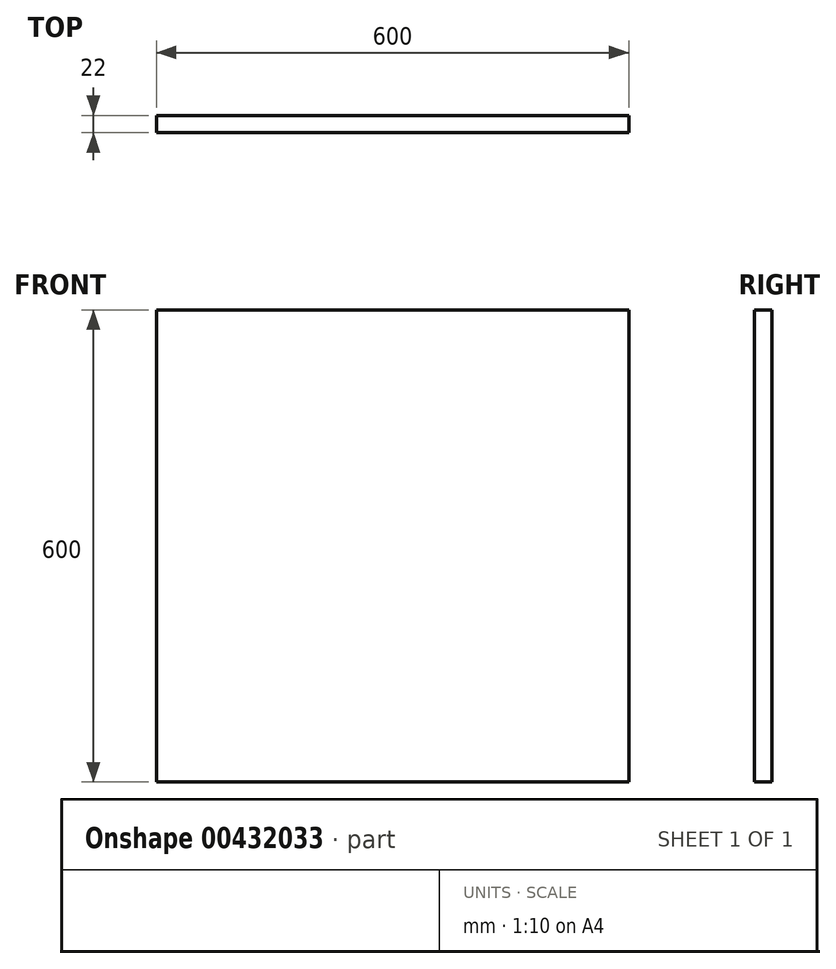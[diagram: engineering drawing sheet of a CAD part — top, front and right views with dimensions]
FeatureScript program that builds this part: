
annotation { "Feature Type Name" : "Feature", "Feature Type Description" : "" }
export const myFeature = defineFeature(function(context is Context, id is Id, definition is map)
    precondition{}
    {
        {
            var Q0;
            Q0=qCreatedBy(makeId("Front.planeOp"),FACE);
            var sketch = newSketch(context, id + "F0", { "sketchPlane" : qUnion([Q0])});
            skLineSegment(sketch, "E0.bottom", {"start": v(0, 0) * mm, "end": v(600, 0) * mm});
            skLineSegment(sketch, "E0.top", {"start": v(0, 600) * mm, "end": v(600, 600) * mm});
            skLineSegment(sketch, "E0.left", {"start": v(0, 0) * mm, "end": v(0, 600) * mm});
            skLineSegment(sketch, "E0.right", {"start": v(600, 0) * mm, "end": v(600, 600) * mm});
            skSolve(sketch);
        }
        {
            var Q0;
            Q0 = qSketchRegion(id + "F0", true);
            extrude(context, id + "F1", {"entities" : qUnion([Q0]), "depth" : 22 * mm});
        }
    });
